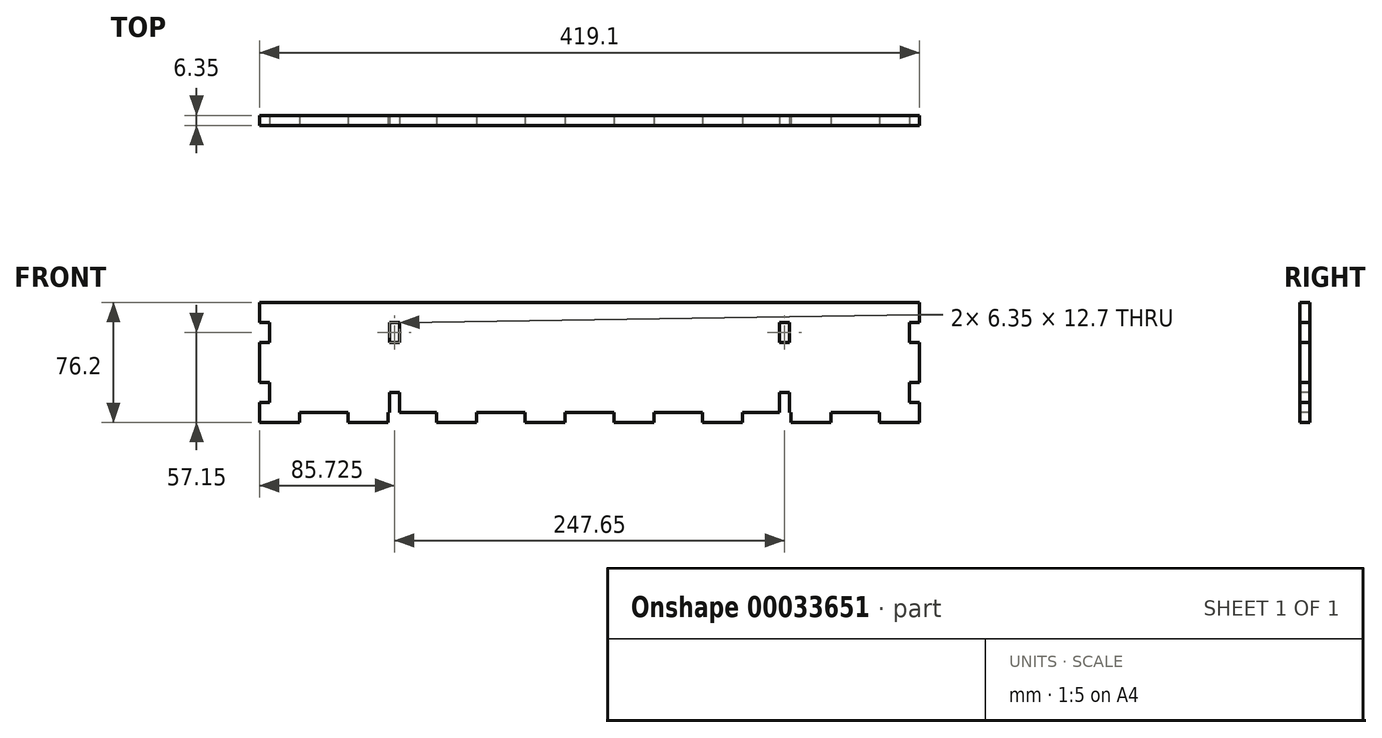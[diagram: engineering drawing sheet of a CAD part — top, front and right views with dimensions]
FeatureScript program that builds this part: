
annotation { "Feature Type Name" : "Feature", "Feature Type Description" : "" }
export const myFeature = defineFeature(function(context is Context, id is Id, definition is map)
    precondition{}
    {
        {
            var Q0;
            Q0=qCreatedBy(makeId("Front.planeOp"),FACE);
            var sketch = newSketch(context, id + "F0", { "sketchPlane" : qUnion([Q0])});
            skLineSegment(sketch, "E0.rect.bottom", {"start": v(-209.55, 38.1) * mm, "end": v(209.55, 38.1) * mm});
            skLineSegment(sketch, "E0.rect.top", {"start": v(-209.55, -38.1) * mm, "end": v(209.55, -38.1) * mm});
            skLineSegment(sketch, "E0.rect.left", {"start": v(-209.55, 38.1) * mm, "end": v(-209.55, -38.1) * mm});
            skLineSegment(sketch, "E0.rect.right", {"start": v(209.55, 38.1) * mm, "end": v(209.55, -38.1) * mm});
            skPoint(sketch, "E0.rect.middle", {"position": v(0, 0) * mm});
            skSolve(sketch);
        }
        {
            var Q0;
            Q0 = qSketchRegion(id + "F0", true);
            extrude(context, id + "F1", {"entities" : qUnion([Q0]), "depth" : 6.35 * mm});
        }
        {
            var Q0;
            Q0=makeQuery(id+"F1.opExtrude","CAP_FACE",FACE,{"disambiguationData":[OSD([sQuery(id+"F0.wireOp",EDGE,"E0.rect.bottom"),sQuery(id+"F0.wireOp",EDGE,"E0.rect.top"),sQuery(id+"F0.wireOp",EDGE,"E0.rect.left"),sQuery(id+"F0.wireOp",EDGE,"E0.rect.right")])],"isStart":false});
            var sketch = newSketch(context, id + "F2", { "sketchPlane" : qUnion([Q0])});
            skLineSegment(sketch, "E1.bottom", {"start": v(-184.15, -38.1) * mm, "end": v(-153.3, -38.1) * mm});
            skLineSegment(sketch, "E1.top", {"start": v(-184.15, -31.75) * mm, "end": v(-153.3, -31.75) * mm});
            skLineSegment(sketch, "E1.left", {"start": v(-184.15, -38.1) * mm, "end": v(-184.15, -31.75) * mm});
            skLineSegment(sketch, "E1.right", {"start": v(-153.3, -38.1) * mm, "end": v(-153.3, -31.75) * mm});
            skLineSegment(sketch, "E2.1.0.0", {"start": v(-127.9, -38.1) * mm, "end": v(-97.06, -38.1) * mm});
            skLineSegment(sketch, "E2.1.0.1", {"start": v(-127.9, -31.75) * mm, "end": v(-97.06, -31.75) * mm});
            skLineSegment(sketch, "E2.1.0.2", {"start": v(-127.9, -38.1) * mm, "end": v(-127.9, -31.75) * mm});
            skLineSegment(sketch, "E2.1.0.3", {"start": v(-97.06, -38.1) * mm, "end": v(-97.06, -31.75) * mm});
            skLineSegment(sketch, "E2.2.0.0", {"start": v(-71.66, -38.1) * mm, "end": v(-40.82, -38.1) * mm});
            skLineSegment(sketch, "E2.2.0.1", {"start": v(-71.66, -31.75) * mm, "end": v(-40.82, -31.75) * mm});
            skLineSegment(sketch, "E2.2.0.2", {"start": v(-71.66, -38.1) * mm, "end": v(-71.66, -31.75) * mm});
            skLineSegment(sketch, "E2.2.0.3", {"start": v(-40.82, -38.1) * mm, "end": v(-40.82, -31.75) * mm});
            skLineSegment(sketch, "E2.3.0.0", {"start": v(-15.42, -38.1) * mm, "end": v(15.42, -38.1) * mm});
            skLineSegment(sketch, "E2.3.0.1", {"start": v(-15.42, -31.75) * mm, "end": v(15.42, -31.75) * mm});
            skLineSegment(sketch, "E2.3.0.2", {"start": v(-15.42, -38.1) * mm, "end": v(-15.42, -31.75) * mm});
            skLineSegment(sketch, "E2.3.0.3", {"start": v(15.42, -38.1) * mm, "end": v(15.42, -31.75) * mm});
            skLineSegment(sketch, "E2.4.0.0", {"start": v(40.82, -38.1) * mm, "end": v(71.66, -38.1) * mm});
            skLineSegment(sketch, "E2.4.0.1", {"start": v(40.82, -31.75) * mm, "end": v(71.66, -31.75) * mm});
            skLineSegment(sketch, "E2.4.0.2", {"start": v(40.82, -38.1) * mm, "end": v(40.82, -31.75) * mm});
            skLineSegment(sketch, "E2.4.0.3", {"start": v(71.66, -38.1) * mm, "end": v(71.66, -31.75) * mm});
            skLineSegment(sketch, "E2.5.0.0", {"start": v(97.06, -38.1) * mm, "end": v(127.9, -38.1) * mm});
            skLineSegment(sketch, "E2.5.0.1", {"start": v(97.06, -31.75) * mm, "end": v(127.9, -31.75) * mm});
            skLineSegment(sketch, "E2.5.0.2", {"start": v(97.06, -38.1) * mm, "end": v(97.06, -31.75) * mm});
            skLineSegment(sketch, "E2.5.0.3", {"start": v(127.9, -38.1) * mm, "end": v(127.9, -31.75) * mm});
            skLineSegment(sketch, "E2.6.0.0", {"start": v(153.3, -38.1) * mm, "end": v(184.15, -38.1) * mm});
            skLineSegment(sketch, "E2.6.0.1", {"start": v(153.3, -31.75) * mm, "end": v(184.15, -31.75) * mm});
            skLineSegment(sketch, "E2.6.0.2", {"start": v(153.3, -38.1) * mm, "end": v(153.3, -31.75) * mm});
            skLineSegment(sketch, "E2.6.0.3", {"start": v(184.15, -38.1) * mm, "end": v(184.15, -31.75) * mm});
            skLineSegment(sketch, "E2.direction1", {"start": v(-184.15, -38.1) * mm, "end": v(-127.9, -38.1) * mm, "construction": true});
            skLineSegment(sketch, "E3.bottom", {"start": v(-209.55, -25.4) * mm, "end": v(-203.2, -25.4) * mm});
            skLineSegment(sketch, "E3.top", {"start": v(-209.55, -12.7) * mm, "end": v(-203.2, -12.7) * mm});
            skLineSegment(sketch, "E3.left", {"start": v(-209.55, -25.4) * mm, "end": v(-209.55, -12.7) * mm});
            skLineSegment(sketch, "E3.right", {"start": v(-203.2, -25.4) * mm, "end": v(-203.2, -12.7) * mm});
            skLineSegment(sketch, "E4.bottom", {"start": v(-209.55, 25.4) * mm, "end": v(-203.2, 25.4) * mm});
            skLineSegment(sketch, "E4.top", {"start": v(-209.55, 12.7) * mm, "end": v(-203.2, 12.7) * mm});
            skLineSegment(sketch, "E4.left", {"start": v(-209.55, 25.4) * mm, "end": v(-209.55, 12.7) * mm});
            skLineSegment(sketch, "E4.right", {"start": v(-203.2, 25.4) * mm, "end": v(-203.2, 12.7) * mm});
            skLineSegment(sketch, "E5", {"start": v(0, 38.1) * mm, "end": v(0, -38.1) * mm, "construction": true});
            skLineSegment(sketch, "E6.MirrorCS", {"start": v(203.2, 25.4) * mm, "end": v(203.2, 12.7) * mm});
            skLineSegment(sketch, "E7.MirrorCS", {"start": v(209.55, -25.4) * mm, "end": v(203.2, -25.4) * mm});
            skLineSegment(sketch, "E8.MirrorCS", {"start": v(209.55, 25.4) * mm, "end": v(209.55, 12.7) * mm});
            skLineSegment(sketch, "E9.MirrorCS", {"start": v(203.2, -25.4) * mm, "end": v(203.2, -12.7) * mm});
            skLineSegment(sketch, "E10.MirrorCS", {"start": v(209.55, -12.7) * mm, "end": v(203.2, -12.7) * mm});
            skLineSegment(sketch, "E11.MirrorCS", {"start": v(209.55, 25.4) * mm, "end": v(203.2, 25.4) * mm});
            skLineSegment(sketch, "E12.MirrorCS", {"start": v(209.55, 12.7) * mm, "end": v(203.2, 12.7) * mm});
            skLineSegment(sketch, "E13.MirrorCS", {"start": v(209.55, -25.4) * mm, "end": v(209.55, -12.7) * mm});
            skSolve(sketch);
        }
        {
            var Q0;
            Q0 = qSketchRegion(id + "F2", true);
            extrude(context, id + "F3", {"entities" : qUnion([Q0]), "operationType" : NewBodyOperationType.REMOVE, "endBound" : BoundingType.THROUGH_ALL, "oppositeDirection" : true, "depth" : 25.4 * mm});
        }
        {
            var Q0;
            Q0=makeQuery(id+"F1.opExtrude","CAP_FACE",FACE,{"disambiguationData":[OSD([sQuery(id+"F0.wireOp",EDGE,"E0.rect.bottom"),sQuery(id+"F0.wireOp",EDGE,"E0.rect.top"),sQuery(id+"F0.wireOp",EDGE,"E0.rect.left"),sQuery(id+"F0.wireOp",EDGE,"E0.rect.right")])],"isStart":false});
            var sketch = newSketch(context, id + "F4", { "sketchPlane" : qUnion([Q0])});
            skLineSegment(sketch, "E14.bottom", {"start": v(-127, -19.05) * mm, "end": v(-120.65, -19.05) * mm});
            skLineSegment(sketch, "E14.top", {"start": v(-127, -31.75) * mm, "end": v(-120.65, -31.75) * mm});
            skLineSegment(sketch, "E14.left", {"start": v(-127, -19.05) * mm, "end": v(-127, -31.75) * mm});
            skLineSegment(sketch, "E14.right", {"start": v(-120.65, -19.05) * mm, "end": v(-120.65, -31.75) * mm});
            skLineSegment(sketch, "E15", {"start": v(0, 38.1) * mm, "end": v(0, -31.75) * mm, "construction": true});
            skLineSegment(sketch, "E16.bottom", {"start": v(-127, 12.7) * mm, "end": v(-120.65, 12.7) * mm});
            skLineSegment(sketch, "E16.top", {"start": v(-127, 25.4) * mm, "end": v(-120.65, 25.4) * mm});
            skLineSegment(sketch, "E16.left", {"start": v(-127, 12.7) * mm, "end": v(-127, 25.4) * mm});
            skLineSegment(sketch, "E16.right", {"start": v(-120.65, 12.7) * mm, "end": v(-120.65, 25.4) * mm});
            skLineSegment(sketch, "E17.MirrorCS", {"start": v(127, 12.7) * mm, "end": v(120.65, 12.7) * mm});
            skLineSegment(sketch, "E18.MirrorCS", {"start": v(120.65, 12.7) * mm, "end": v(120.65, 25.4) * mm});
            skLineSegment(sketch, "E19.MirrorCS", {"start": v(127, 12.7) * mm, "end": v(127, 25.4) * mm});
            skLineSegment(sketch, "E20.MirrorCS", {"start": v(127, 25.4) * mm, "end": v(120.65, 25.4) * mm});
            skLineSegment(sketch, "E21.MirrorCS", {"start": v(120.65, -19.05) * mm, "end": v(120.65, -31.75) * mm});
            skLineSegment(sketch, "E22.MirrorCS", {"start": v(127, -19.05) * mm, "end": v(127, -31.75) * mm});
            skLineSegment(sketch, "E23.MirrorCS", {"start": v(127, -19.05) * mm, "end": v(120.65, -19.05) * mm});
            skLineSegment(sketch, "E24.MirrorCS", {"start": v(127, -31.75) * mm, "end": v(120.65, -31.75) * mm});
            skSolve(sketch);
        }
        {
            var Q0;
            Q0 = qSketchRegion(id + "F4", true);
            extrude(context, id + "F5", {"entities" : qUnion([Q0]), "operationType" : NewBodyOperationType.REMOVE, "endBound" : BoundingType.THROUGH_ALL, "oppositeDirection" : true, "depth" : 25.4 * mm});
        }
    });
